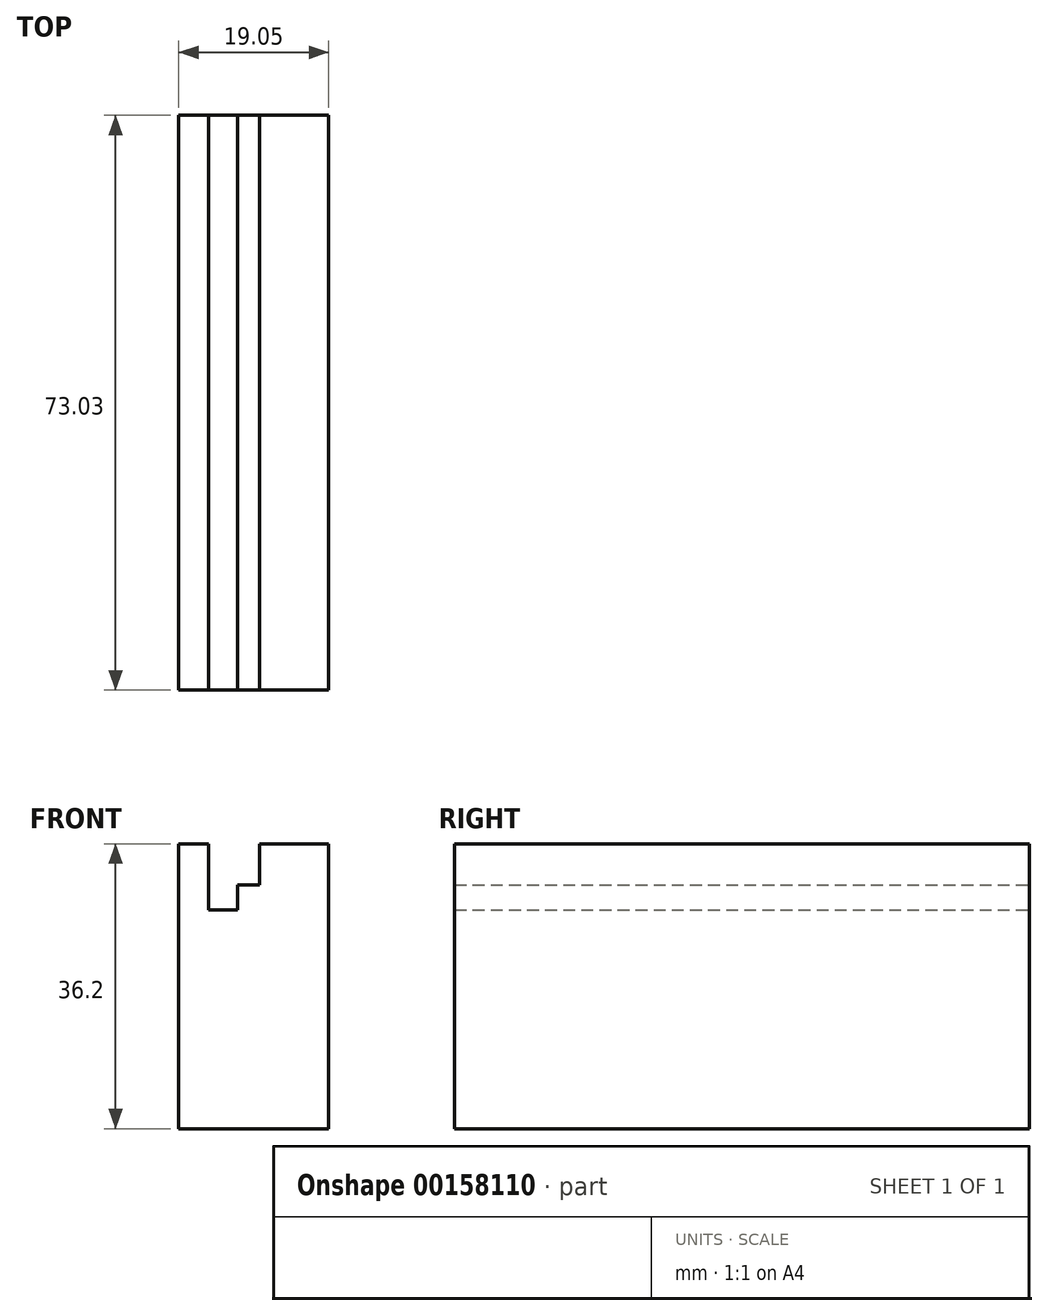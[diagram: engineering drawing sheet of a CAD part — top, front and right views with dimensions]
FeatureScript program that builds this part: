
annotation { "Feature Type Name" : "Feature", "Feature Type Description" : "" }
export const myFeature = defineFeature(function(context is Context, id is Id, definition is map)
    precondition{}
    {
        {
            var Q0;
            Q0=qCreatedBy(makeId("Front.planeOp"),FACE);
            var sketch = newSketch(context, id + "F0", { "sketchPlane" : qUnion([Q0])});
            skLineSegment(sketch, "E0", {"start": v(0, 0) * mm, "end": v(3.81, 0) * mm});
            skLineSegment(sketch, "E1", {"start": v(3.81, 0) * mm, "end": v(3.81, -8.43) * mm});
            skLineSegment(sketch, "E2", {"start": v(3.81, -8.43) * mm, "end": v(7.5, -8.43) * mm});
            skLineSegment(sketch, "E3", {"start": v(7.5, -8.43) * mm, "end": v(7.5, -5.22) * mm});
            skLineSegment(sketch, "E4", {"start": v(7.5, -5.22) * mm, "end": v(10.29, -5.22) * mm});
            skLineSegment(sketch, "E5", {"start": v(10.29, -5.22) * mm, "end": v(10.29, 0) * mm});
            skLineSegment(sketch, "E6", {"start": v(10.29, 0) * mm, "end": v(19.05, 0) * mm});
            skLineSegment(sketch, "E7", {"start": v(19.05, 0) * mm, "end": v(19.05, -36.2) * mm});
            skLineSegment(sketch, "E8", {"start": v(19.05, -36.2) * mm, "end": v(0, -36.2) * mm});
            skLineSegment(sketch, "E9", {"start": v(0, -36.2) * mm, "end": v(0, 0) * mm});
            skSolve(sketch);
        }
        {
            var Q0;
            Q0 = qSketchRegion(id + "F0", true);
            extrude(context, id + "F1", {"entities" : qUnion([Q0]), "depth" : 73.02 * mm});
        }
    });
